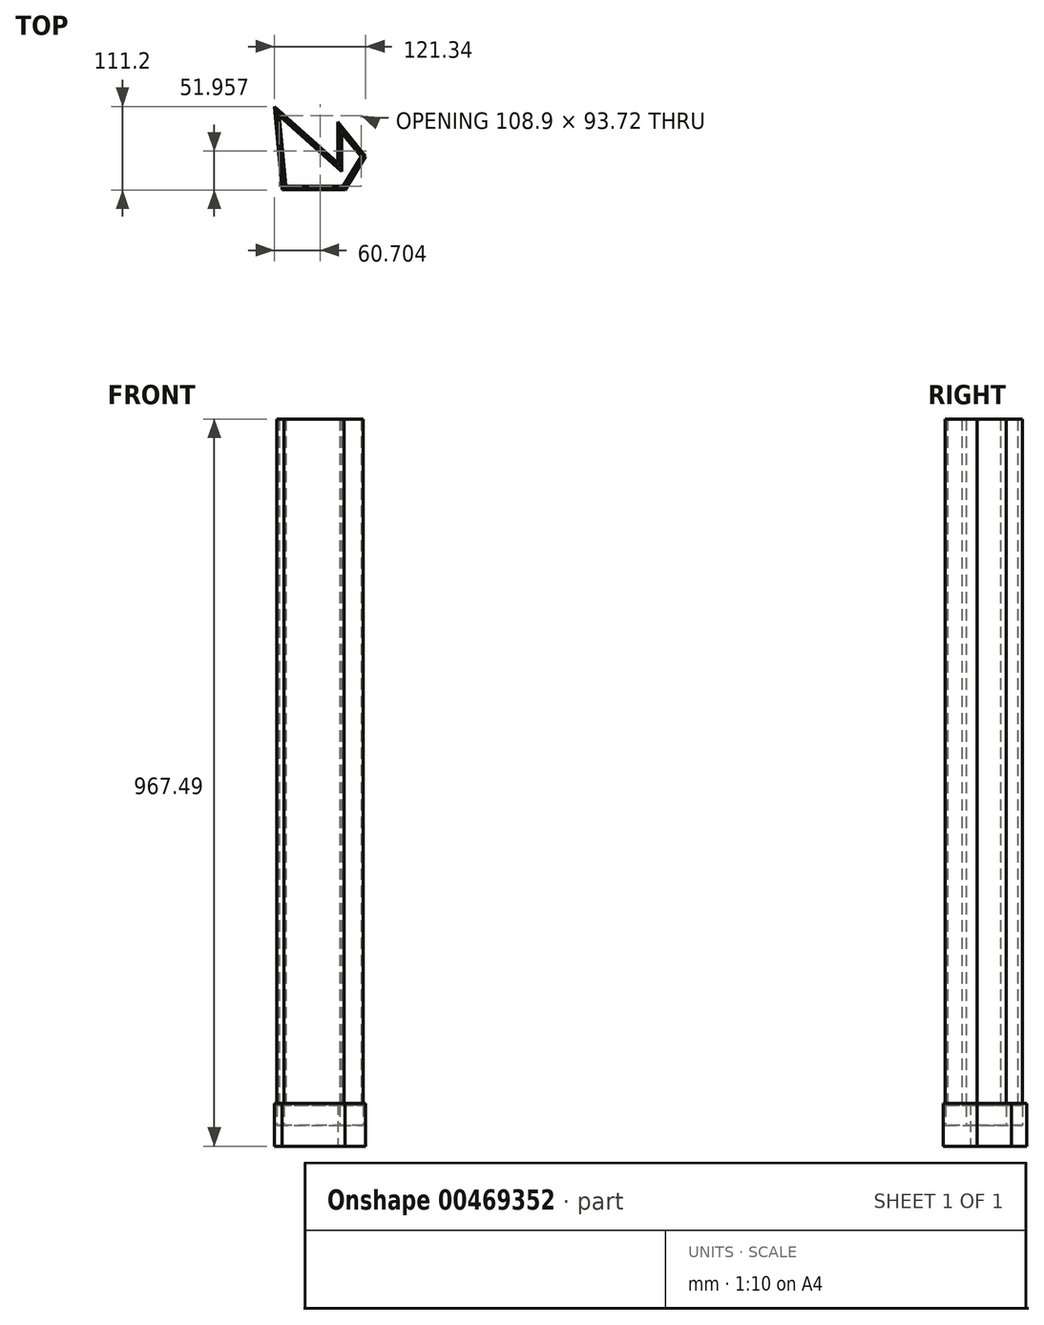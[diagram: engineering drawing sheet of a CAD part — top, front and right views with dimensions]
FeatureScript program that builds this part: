
annotation { "Feature Type Name" : "Feature", "Feature Type Description" : "" }
export const myFeature = defineFeature(function(context is Context, id is Id, definition is map)
    precondition{}
    {
        {
            var Q0;
            Q0=qCreatedBy(makeId("Top.planeOp"),FACE);
            var sketch = newSketch(context, id + "F0", { "sketchPlane" : qUnion([Q0])});
            skLineSegment(sketch, "E0", {"start": v(-57.1, -52.64) * mm, "end": v(-67.43, 58.06) * mm});
            skLineSegment(sketch, "E1", {"start": v(-67.43, 58.06) * mm, "end": v(17.09, -17.26) * mm});
            skLineSegment(sketch, "E2", {"start": v(17.09, -17.26) * mm, "end": v(17.09, 37.6) * mm});
            skLineSegment(sketch, "E3", {"start": v(17.09, 37.6) * mm, "end": v(53.91, -8.21) * mm});
            skLineSegment(sketch, "E4", {"start": v(53.91, -8.21) * mm, "end": v(26.61, -53.14) * mm});
            skLineSegment(sketch, "E5", {"start": v(26.61, -53.14) * mm, "end": v(-57.1, -52.64) * mm});
            skSolve(sketch);
        }
        {
            var Q0;
            Q0=makeQuery(id+"F0.imprint","IMPRINT",FACE,{"disambiguationData":[TD([[makeQuery(id+"F0.imprint","IMPRINT",EDGE,{"derivedFrom":sQuery(id+"F0.wireOp",EDGE,"E0")}),-1.0]])]});
            extrude(context, id + "F1", {"entities" : qUnion([Q0]), "depth" : 56.64 * mm});
        }
        {
            var Q0;
            Q0=makeQuery(id+"F1.opExtrude","CAP_FACE",FACE,{"disambiguationData":[OSD([sQuery(id+"F0.wireOp",EDGE,"E0"),sQuery(id+"F0.wireOp",EDGE,"E1"),sQuery(id+"F0.wireOp",EDGE,"E2"),sQuery(id+"F0.wireOp",EDGE,"E3"),sQuery(id+"F0.wireOp",EDGE,"E4"),sQuery(id+"F0.wireOp",EDGE,"E5")])],"isStart":false});
            shell(context, id + "F2", {"entities" : qUnion([Q0]), "thickness" : 2.54 * mm});
        }
        {
            var Q0;
            Q0=makeQuery(id+"F2.opShell","OFFSET_FACE",FACE,{"disambiguationData":[OSD([sQuery(id+"F0.wireOp",EDGE,"E0"),sQuery(id+"F0.wireOp",EDGE,"E1"),sQuery(id+"F0.wireOp",EDGE,"E2"),sQuery(id+"F0.wireOp",EDGE,"E3"),sQuery(id+"F0.wireOp",EDGE,"E4"),sQuery(id+"F0.wireOp",EDGE,"E5")])]});
            extrude(context, id + "F3", {"entities" : qUnion([Q0]), "operationType" : NewBodyOperationType.ADD, "depth" : 964.95 * mm});
        }
        {
            var Q0;
            Q0=makeQuery(id+"F3.opExtrude","CAP_FACE",FACE,{"disambiguationData":[OSD([sQuery(id+"F0.wireOp",EDGE,"E0"),sQuery(id+"F0.wireOp",EDGE,"E1"),sQuery(id+"F0.wireOp",EDGE,"E2"),sQuery(id+"F0.wireOp",EDGE,"E3"),sQuery(id+"F0.wireOp",EDGE,"E4"),sQuery(id+"F0.wireOp",EDGE,"E5")])],"isStart":false});
            shell(context, id + "F4", {"entities" : qUnion([Q0]), "thickness" : 2.54 * mm});
        }
        {
            var Q0;
            Q0 = qSketchRegion(id + "F0", true);
            var Q1;
            {var subQ0=sQuery(id+"F0.wireOp",EDGE,"E5");var subQ1=sQuery(id+"F0.wireOp",EDGE,"E4");var subQ2=sQuery(id+"F0.wireOp",EDGE,"E3");var subQ3=sQuery(id+"F0.wireOp",EDGE,"E2");var subQ4=sQuery(id+"F0.wireOp",EDGE,"E1");var subQ5=sQuery(id+"F0.wireOp",EDGE,"E0");Q1=makeQuery(id+"F4.opShell","OFFSET_FACE",FACE,{"disambiguationData":[OSD([subQ5,subQ4,subQ3,subQ2,subQ1,subQ0]),TDD([makeQuery(id+"F1.opExtrude","CAP_FACE",FACE,{"disambiguationData":[OSD([subQ5,subQ4,subQ3,subQ2,subQ1,subQ0])],"isStart":true})])]});}
            extrude(context, id + "F5", {"entities" : qUnion([Q0, Q1]), "operationType" : NewBodyOperationType.ADD, "depth" : 25.4 * mm});
        }
    });
